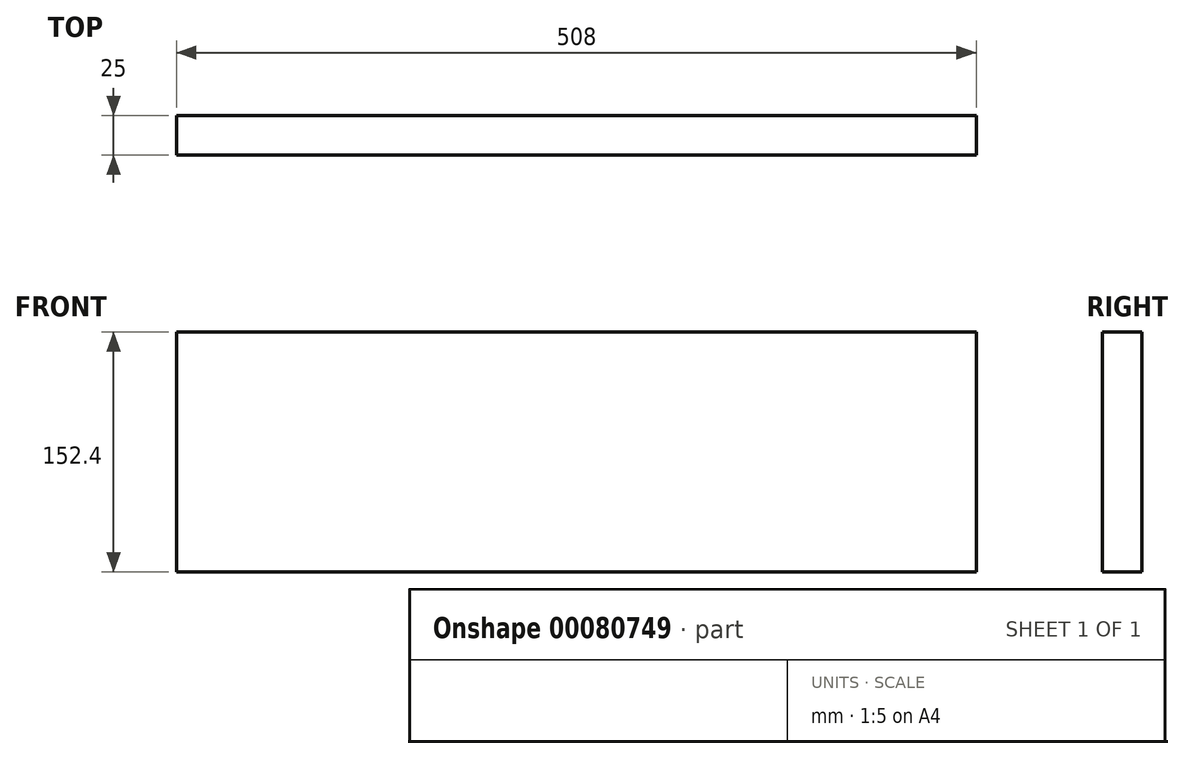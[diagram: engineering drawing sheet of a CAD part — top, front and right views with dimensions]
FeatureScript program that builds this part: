
annotation { "Feature Type Name" : "Feature", "Feature Type Description" : "" }
export const myFeature = defineFeature(function(context is Context, id is Id, definition is map)
    precondition{}
    {
        {
            var Q0;
            Q0=qCreatedBy(makeId("Front.planeOp"),FACE);
            var sketch = newSketch(context, id + "F0", { "sketchPlane" : qUnion([Q0])});
            skLineSegment(sketch, "E0.bottom", {"start": v(254, 76.2) * mm, "end": v(-254, 76.2) * mm});
            skLineSegment(sketch, "E0.top", {"start": v(254, -76.2) * mm, "end": v(-254, -76.2) * mm});
            skLineSegment(sketch, "E0.left", {"start": v(254, 76.2) * mm, "end": v(254, -76.2) * mm});
            skLineSegment(sketch, "E0.right", {"start": v(-254, 76.2) * mm, "end": v(-254, -76.2) * mm});
            skPoint(sketch, "E0.middle", {"position": v(0, 0) * mm});
            skSolve(sketch);
        }
        {
            var Q0;
            Q0=makeQuery(id+"F0.imprint","IMPRINT",FACE,{"disambiguationData":[TD([[makeQuery(id+"F0.imprint","IMPRINT",EDGE,{"derivedFrom":sQuery(id+"F0.wireOp",EDGE,"E0.bottom")}),1.0]])]});
            extrude(context, id + "F1", {"entities" : qUnion([Q0]), "depth" : 25 * mm});
        }
    });
